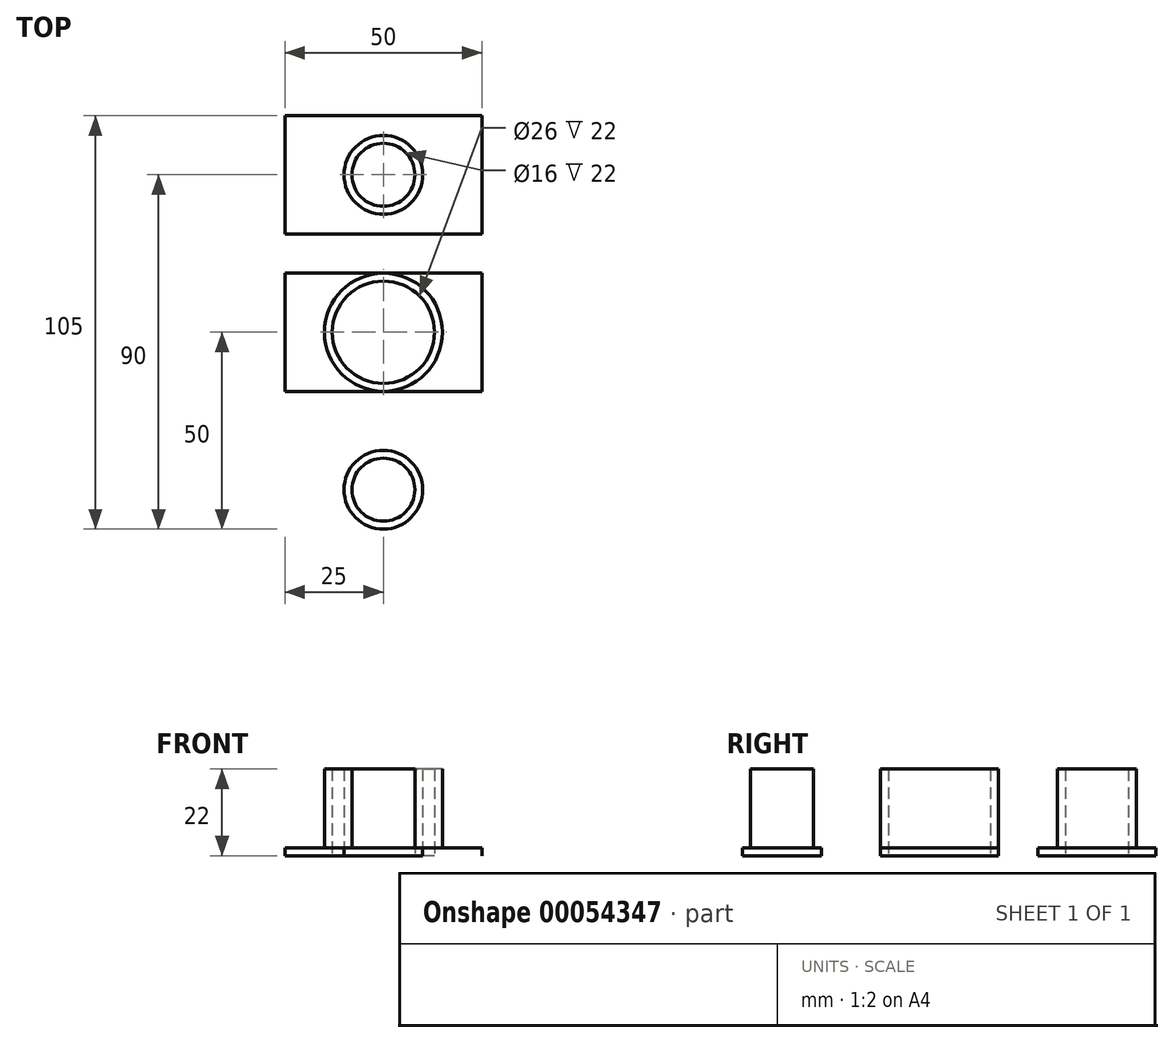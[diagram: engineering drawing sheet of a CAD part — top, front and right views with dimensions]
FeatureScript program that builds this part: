
annotation { "Feature Type Name" : "Feature", "Feature Type Description" : "" }
export const myFeature = defineFeature(function(context is Context, id is Id, definition is map)
    precondition{}
    {
        {
            var Q0;
            Q0=qCreatedBy(makeId("Top.planeOp"),FACE);
            var sketch = newSketch(context, id + "F0", { "sketchPlane" : qUnion([Q0])});
            skLineSegment(sketch, "E0.rect.bottom", {"start": v(-25, 15) * mm, "end": v(25, 15) * mm});
            skLineSegment(sketch, "E0.rect.top", {"start": v(-25, -15) * mm, "end": v(25, -15) * mm});
            skLineSegment(sketch, "E0.rect.left", {"start": v(-25, 15) * mm, "end": v(-25, -15) * mm});
            skLineSegment(sketch, "E0.rect.right", {"start": v(25, 15) * mm, "end": v(25, -15) * mm});
            skPoint(sketch, "E0.rect.middle", {"position": v(0, 0) * mm});
            skCircle(sketch, "E1", {"center": v(0, 0) * mm, "radius": 15 * mm});
            skCircle(sketch, "E2", {"center": v(0, 0) * mm, "radius": 13 * mm});
            skLineSegment(sketch, "E3.rect.bottom", {"start": v(-25, 55) * mm, "end": v(25, 55) * mm});
            skLineSegment(sketch, "E3.rect.top", {"start": v(-25, 25) * mm, "end": v(25, 25) * mm});
            skLineSegment(sketch, "E3.rect.left", {"start": v(-25, 55) * mm, "end": v(-25, 25) * mm});
            skLineSegment(sketch, "E3.rect.right", {"start": v(25, 55) * mm, "end": v(25, 25) * mm});
            skPoint(sketch, "E3.rect.middle", {"position": v(0, 40) * mm});
            skCircle(sketch, "E4", {"center": v(0, 40) * mm, "radius": 10 * mm});
            skCircle(sketch, "E5", {"center": v(0, 40) * mm, "radius": 8 * mm});
            skCircle(sketch, "E6.MirrorC", {"center": v(0, -40) * mm, "radius": 8 * mm});
            skCircle(sketch, "E7.MirrorC", {"center": v(0, -40) * mm, "radius": 10 * mm});
            skLineSegment(sketch, "E8.MirrorCS", {"start": v(-25, -25) * mm, "end": v(25, -25) * mm});
            skLineSegment(sketch, "E9.MirrorCS", {"start": v(-25, -55) * mm, "end": v(-25, -25) * mm});
            skLineSegment(sketch, "E10.MirrorCS", {"start": v(25, -55) * mm, "end": v(25, -25) * mm});
            skLineSegment(sketch, "E11.MirrorCS", {"start": v(-25, -55) * mm, "end": v(25, -55) * mm});
            skSolve(sketch);
        }
        {
            var Q0;
            {var subQ0=sQuery(id+"F0.wireOp",EDGE,"E0.rect.left");Q0=makeQuery(id+"F0.imprint","IMPRINT",FACE,{"disambiguationData":[TD([[makeQuery(id+"F0.imprint","IMPRINT",EDGE,{"derivedFrom":subQ0}),1.0]])]});}
            var Q1;
            {var subQ0=sQuery(id+"F0.wireOp",EDGE,"E0.rect.right");Q1=makeQuery(id+"F0.imprint","IMPRINT",FACE,{"disambiguationData":[TD([[makeQuery(id+"F0.imprint","IMPRINT",EDGE,{"derivedFrom":subQ0}),-1.0]])]});}
            var Q2;
            Q2=makeQuery(id+"F0.imprint","IMPRINT",FACE,{"disambiguationData":[TD([[makeQuery(id+"F0.imprint","IMPRINT",EDGE,{"derivedFrom":sQuery(id+"F0.wireOp",EDGE,"E3.rect.bottom")}),-1.0]])]});
            var Q3;
            Q3=makeQuery(id+"F0.imprint","IMPRINT",FACE,{"disambiguationData":[TD([[makeQuery(id+"F0.imprint","IMPRINT",EDGE,{"derivedFrom":sQuery(id+"F0.wireOp",EDGE,"E7.MirrorC")}),1.0]])]});
            extrude(context, id + "F1", {"entities" : qUnion([Q0, Q1, Q2, Q3]), "depth" : 2 * mm});
        }
        {
            var Q0;
            Q0=makeQuery(id+"F0.imprint","IMPRINT",FACE,{"disambiguationData":[TD([[makeQuery(id+"F0.imprint","IMPRINT",EDGE,{"derivedFrom":sQuery(id+"F0.wireOp",EDGE,"E1")}),1.0]])]});
            var Q1;
            Q1=makeQuery(id+"F0.imprint","IMPRINT",FACE,{"disambiguationData":[TD([[makeQuery(id+"F0.imprint","IMPRINT",EDGE,{"derivedFrom":sQuery(id+"F0.wireOp",EDGE,"E4")}),1.0]])]});
            var Q2;
            Q2=makeQuery(id+"F0.imprint","IMPRINT",FACE,{"disambiguationData":[TD([[makeQuery(id+"F0.imprint","IMPRINT",EDGE,{"derivedFrom":sQuery(id+"F0.wireOp",EDGE,"E6.MirrorC")}),1.0]])]});
            extrude(context, id + "F2", {"entities" : qUnion([Q0, Q1, Q2]), "operationType" : NewBodyOperationType.ADD, "depth" : 22 * mm});
        }
    });
